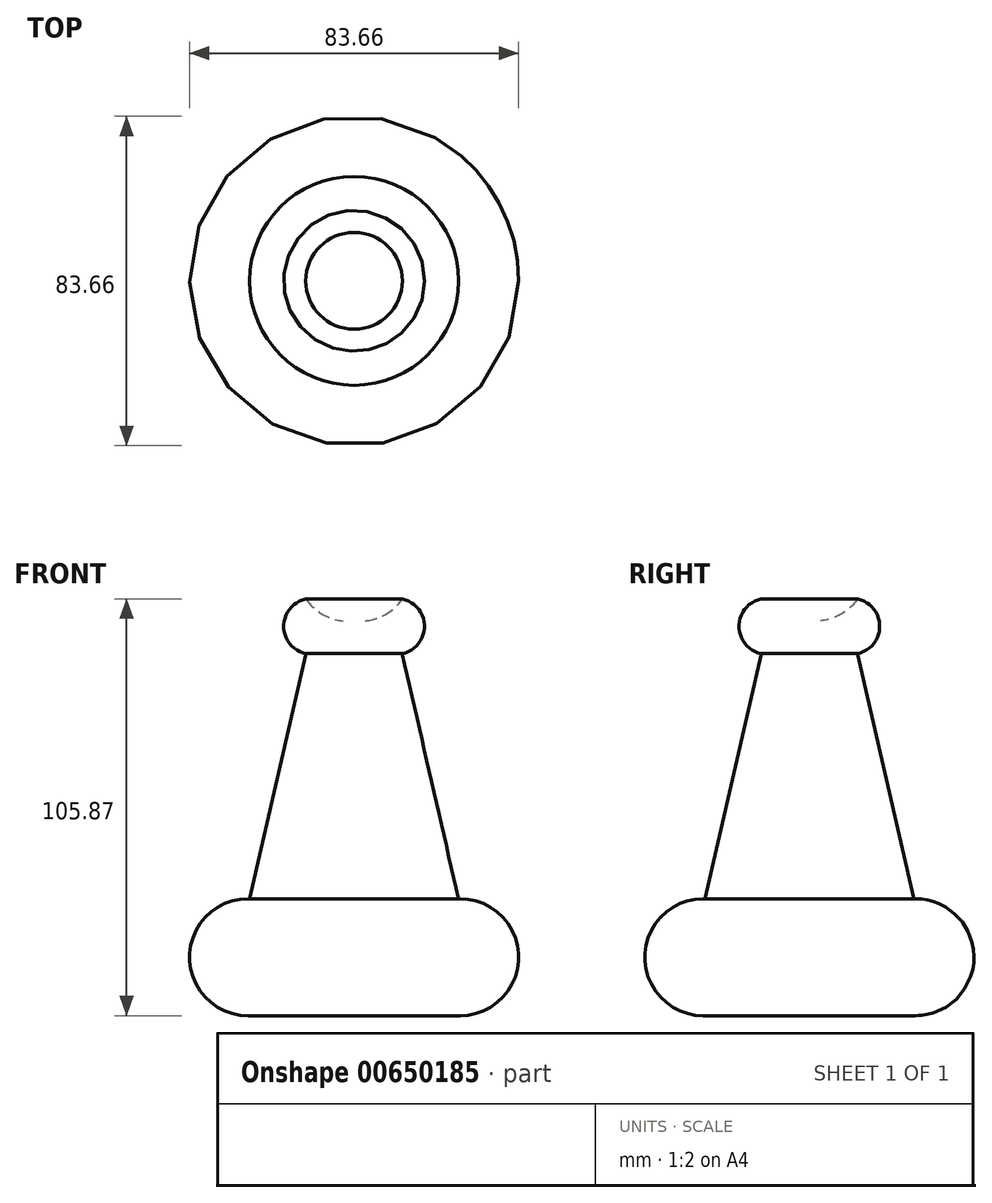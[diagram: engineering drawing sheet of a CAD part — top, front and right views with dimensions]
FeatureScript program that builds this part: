
annotation { "Feature Type Name" : "Feature", "Feature Type Description" : "" }
export const myFeature = defineFeature(function(context is Context, id is Id, definition is map)
    precondition{}
    {
        {
            var Q0;
            Q0=qCreatedBy(makeId("Front.planeOp"),FACE);
            var sketch = newSketch(context, id + "F0", { "sketchPlane" : qUnion([Q0])});
            skLineSegment(sketch, "E0", {"start": v(-26.98, -52.84) * mm, "end": v(0, -52.84) * mm});
            skLineSegment(sketch, "E1", {"start": v(0, -52.84) * mm, "end": v(0, 73.94) * mm});
            skLineSegment(sketch, "E2", {"start": v(0, 73.94) * mm, "end": v(-12.21, 39.14) * mm});
            skLineSegment(sketch, "E3", {"start": v(-12.21, 39.14) * mm, "end": v(-26.54, -23.15) * mm});
            skLineSegment(sketch, "E4", {"start": v(-26.54, -23.15) * mm, "end": v(-26.98, -52.84) * mm});
            skArc(sketch, "E5", {"start": v(-26.54, -23.15) * mm, "mid": v(-41.82, -37.77) * mm, "end": v(-26.98, -52.84) * mm});
            skArc(sketch, "E6", {"start": v(0, 73.94) * mm, "mid": v(-12.9, 67.46) * mm, "end": v(-12.28, 53.03) * mm});
            skArc(sketch, "E7", {"start": v(-12.28, 53.03) * mm, "mid": v(-17.88, 46.06) * mm, "end": v(-12.21, 39.14) * mm});
            skSolve(sketch);
        }
        {
            var Q0;
            Q0=qCreatedBy(makeId("Front.planeOp"),FACE);
            var sketch = newSketch(context, id + "F1", { "sketchPlane" : qUnion([Q0])});
            skLineSegment(sketch, "E8", {"start": v(0, -60.88) * mm, "end": v(0, 48.5) * mm});
            skSolve(sketch);
        }
        {
            var Q0;
            Q0=makeQuery(id+"F0.imprint","IMPRINT",FACE,{"disambiguationData":[TD([[makeQuery(id+"F0.imprint","IMPRINT",EDGE,{"derivedFrom":sQuery(id+"F0.wireOp",EDGE,"E0")}),1.0]])]});
            var Q1;
            Q1=makeQuery(id+"F0.imprint","IMPRINT",FACE,{"disambiguationData":[TD([[makeQuery(id+"F0.imprint","IMPRINT",EDGE,{"derivedFrom":sQuery(id+"F0.wireOp",EDGE,"E2")}),-1.0]])]});
            var Q2;
            Q2=makeQuery(id+"F0.imprint","IMPRINT",FACE,{"disambiguationData":[TD([[makeQuery(id+"F0.imprint","IMPRINT",EDGE,{"derivedFrom":sQuery(id+"F0.wireOp",EDGE,"E4")}),-1.0]])]});
            var Q3;
            Q3=sQuery(id+"F0.wireOp",EDGE,"E0");
            var Q4;
            Q4=sQuery(id+"F0.wireOp",EDGE,"E5");
            var Q5;
            Q5=sQuery(id+"F0.wireOp",EDGE,"E3");
            var Q6;
            Q6=sQuery(id+"F0.wireOp",EDGE,"E7");
            var Q7;
            Q7=sQuery(id+"F0.wireOp",EDGE,"E6");
            var Q8;
            Q8=sQuery(id+"F1.wireOp",EDGE,"E8");
            revolve(context, id + "F2", {"bodyType" : ToolBodyType.SURFACE, "entities" : qUnion([Q0, Q1, Q2]), "surfaceEntities" : qUnion([Q3, Q4, Q5, Q6, Q7]), "axis" : qUnion([Q8]), "revolveType" : RevolveType.FULL});
        }
    });
